FCSTD DOCUMENT  (FreeCAD 0.18R4 (GitTag))
Label: PLD1_stepper_side
License: All rights reserved
LicenseURL: http://en.wikipedia.org/wiki/All_rights_reserved
objects: Sketcher::SketchObject×1, PartDesign::Body×1
note: 2 computed .brp shape members not serialized (recipe doc carries the construction recipe); baked Part::Feature solids carry a one-line shape summary decoded from their .brp

FEATURE [Sketcher::SketchObject] Sketch
  MapMode = 5
  Support = -> [XY_Plane]
  sketch-geometry (69):
    g0: LineSegment StartX=-44 StartY=101.225 StartZ=0 EndX=0 EndY=101.225 EndZ=0
    g1: LineSegment StartX=0 StartY=101.225 StartZ=0 EndX=0 EndY=-101.225 EndZ=0
    g2: LineSegment StartX=0 StartY=-101.225 StartZ=0 EndX=-44 EndY=-101.225 EndZ=0
    g3: LineSegment StartX=-44 StartY=-101.225 StartZ=0 EndX=-44 EndY=101.225 EndZ=0
    g4: LineSegment StartX=-120.788 StartY=76.56 StartZ=0 EndX=-44 EndY=76.56 EndZ=0
    g5: LineSegment StartX=-44 StartY=76.56 StartZ=0 EndX=-44 EndY=-76.55 EndZ=0
    g6: LineSegment StartX=-44 StartY=-76.55 StartZ=0 EndX=-120.788 EndY=-76.55 EndZ=0
    g7: LineSegment StartX=-120.788 StartY=-76.55 StartZ=0 EndX=-120.788 EndY=76.56 EndZ=0
    g8: LineSegment StartX=0 StartY=155.225 StartZ=0 EndX=150 EndY=155.225 EndZ=0
    g9: LineSegment StartX=150 StartY=155.225 StartZ=0 EndX=150 EndY=151.225 EndZ=0
    g10: LineSegment StartX=150 StartY=151.225 StartZ=0 EndX=0 EndY=151.225 EndZ=0
    g11: LineSegment StartX=0 StartY=151.225 StartZ=0 EndX=0 EndY=155.225 EndZ=0
    g12: LineSegment StartX=-44 StartY=95.225 StartZ=0 EndX=0 EndY=95.225 EndZ=0
    g13: LineSegment StartX=0 StartY=95.225 StartZ=0 EndX=0 EndY=87.225 EndZ=0
    g14: LineSegment StartX=0 StartY=87.225 StartZ=0 EndX=-44 EndY=87.225 EndZ=0
    g15: LineSegment StartX=-44 StartY=87.225 StartZ=0 EndX=-44 EndY=95.225 EndZ=0
    g16: LineSegment StartX=0 StartY=66.725 StartZ=0 EndX=94 EndY=66.725 EndZ=0
    g17: LineSegment StartX=94 StartY=66.725 StartZ=0 EndX=94 EndY=31.725 EndZ=0
    g18: LineSegment StartX=94 StartY=31.725 StartZ=0 EndX=0 EndY=31.725 EndZ=0
    g19: LineSegment StartX=0 StartY=31.725 StartZ=0 EndX=0 EndY=66.725 EndZ=0
    g20: LineSegment StartX=94 StartY=52.225 StartZ=0 EndX=97 EndY=52.225 EndZ=0
    g21: LineSegment StartX=97 StartY=52.225 StartZ=0 EndX=97 EndY=46.225 EndZ=0
    g22: LineSegment StartX=97 StartY=46.225 StartZ=0 EndX=94 EndY=46.225 EndZ=0
    g23: LineSegment StartX=94 StartY=46.225 StartZ=0 EndX=94 EndY=52.225 EndZ=0
    g24: LineSegment StartX=97 StartY=59.225 StartZ=0 EndX=127 EndY=59.225 EndZ=0
    g25: LineSegment StartX=127 StartY=59.225 StartZ=0 EndX=127 EndY=39.225 EndZ=0
    g26: LineSegment StartX=127 StartY=39.225 StartZ=0 EndX=97 EndY=39.225 EndZ=0
    g27: LineSegment StartX=97 StartY=39.225 StartZ=0 EndX=97 EndY=59.225 EndZ=0
    g28: LineSegment StartX=135.919 StartY=67.225 StartZ=0 EndX=141.117 EndY=67.225 EndZ=0
    g29: LineSegment StartX=141.117 StartY=67.225 StartZ=0 EndX=141.117 EndY=31.225 EndZ=0
    g30: LineSegment StartX=141.117 StartY=31.225 StartZ=0 EndX=135.919 EndY=31.225 EndZ=0
    g31: LineSegment StartX=135.919 StartY=31.225 StartZ=0 EndX=135.919 EndY=67.225 EndZ=0
    g32: LineSegment StartX=135.919 StartY=142.225 StartZ=0 EndX=141.117 EndY=142.225 EndZ=0
    g33: LineSegment StartX=141.117 StartY=142.225 StartZ=0 EndX=141.117 EndY=67.225 EndZ=0
    g34: LineSegment StartX=141.117 StartY=67.225 StartZ=0 EndX=135.919 EndY=67.225 EndZ=0
    g35: LineSegment StartX=135.919 StartY=67.225 StartZ=0 EndX=135.919 EndY=142.225 EndZ=0
    g36: LineSegment StartX=96.6033 StartY=114.725 StartZ=0 EndX=126.603 EndY=114.725 EndZ=0
    g37: LineSegment StartX=126.603 StartY=114.725 StartZ=0 EndX=126.603 EndY=94.725 EndZ=0
    g38: LineSegment StartX=126.603 StartY=94.725 StartZ=0 EndX=96.6033 EndY=94.725 EndZ=0
    g39: LineSegment StartX=96.6033 StartY=94.725 StartZ=0 EndX=96.6033 EndY=114.725 EndZ=0
    g40: LineSegment StartX=43.1033 StartY=125.725 StartZ=0 EndX=93.6033 EndY=125.725 EndZ=0
    g41: LineSegment StartX=93.6033 StartY=125.725 StartZ=0 EndX=93.6033 EndY=83.725 EndZ=0
    g42: LineSegment StartX=93.6033 StartY=83.725 StartZ=0 EndX=43.1033 EndY=83.725 EndZ=0
    g43: LineSegment StartX=43.1033 StartY=83.725 StartZ=0 EndX=43.1033 EndY=125.725 EndZ=0
    g44: LineSegment StartX=150 StartY=151.225 StartZ=0 EndX=146 EndY=151.225 EndZ=0
    g45: LineSegment StartX=146 StartY=151.225 StartZ=0 EndX=146 EndY=21.225 EndZ=0
    g46: LineSegment StartX=146 StartY=21.225 StartZ=0 EndX=150 EndY=21.225 EndZ=0
    g47: LineSegment StartX=150 StartY=21.225 StartZ=0 EndX=150 EndY=151.225 EndZ=0
    g48: LineSegment StartX=43.1033 StartY=135.725 StartZ=0 EndX=93.6033 EndY=135.725 EndZ=0
    g49: LineSegment StartX=93.6033 StartY=135.725 StartZ=0 EndX=93.6033 EndY=125.725 EndZ=0
    g50: LineSegment StartX=93.6033 StartY=125.725 StartZ=0 EndX=43.1033 EndY=125.725 EndZ=0
    g51: LineSegment StartX=43.1033 StartY=125.725 StartZ=0 EndX=43.1033 EndY=135.725 EndZ=0
    g52: LineSegment StartX=44.3291 StartY=151.225 StartZ=0 EndX=44.3291 EndY=135.725 EndZ=0
    g53: LineSegment StartX=-103.974 StartY=186.345 StartZ=0 EndX=-68.9742 EndY=186.345 EndZ=0
    g54: LineSegment StartX=-68.9742 StartY=186.345 StartZ=0 EndX=-68.9742 EndY=130.045 EndZ=0
    g55: LineSegment StartX=-68.9742 StartY=130.045 StartZ=0 EndX=-103.974 EndY=130.045 EndZ=0
    g56: LineSegment StartX=-103.974 StartY=130.045 StartZ=0 EndX=-103.974 EndY=186.345 EndZ=0
    g57: LineSegment StartX=-82.7742 StartY=130.045 StartZ=0 EndX=-67.7742 EndY=130.045 EndZ=0
    g58: LineSegment StartX=-67.7742 StartY=130.045 StartZ=0 EndX=-67.7742 EndY=119.045 EndZ=0
    g59: LineSegment StartX=-67.7742 StartY=119.045 StartZ=0 EndX=-82.7742 EndY=119.045 EndZ=0
    g60: LineSegment StartX=-82.7742 StartY=119.045 StartZ=0 EndX=-82.7742 EndY=130.045 EndZ=0
    g61: LineSegment StartX=-218.667 StartY=182.94 StartZ=0 EndX=-118.667 EndY=182.94 EndZ=0
    g62: LineSegment StartX=-118.667 StartY=182.94 StartZ=0 EndX=-118.667 EndY=132.94 EndZ=0
    g63: LineSegment StartX=-118.667 StartY=132.94 StartZ=0 EndX=-218.667 EndY=132.94 EndZ=0
    g64: LineSegment StartX=-218.667 StartY=132.94 StartZ=0 EndX=-218.667 EndY=182.94 EndZ=0
    g65: LineSegment StartX=0 StartY=81.225 StartZ=0 EndX=4 EndY=81.225 EndZ=0
    g66: LineSegment StartX=4 StartY=81.225 StartZ=0 EndX=4 EndY=151.225 EndZ=0
    g67: LineSegment StartX=4 StartY=151.225 StartZ=0 EndX=0 EndY=151.225 EndZ=0
    g68: LineSegment StartX=0 StartY=151.225 StartZ=0 EndX=0 EndY=81.225 EndZ=0
  constraints (199):
    c: Coincident(g0,g1)
    c: Coincident(g1,g2)
    c: Coincident(g2,g3)
    c: Coincident(g3,g0)
    c: Horizontal(g0)
    c: Horizontal(g2)
    c: Vertical(g1)
    c: Vertical(g3)
    c: DistanceX(g0,g0) = 44
    c: DistanceX(g-1,g0) = 0
    c: DistanceY(g2,g0) = 202.45  '202.45'
    c: DistanceY(g1,g-1) = 101.225
    c: Coincident(g4,g5)
    c: Coincident(g5,g6)
    c: Coincident(g6,g7)
    c: Coincident(g7,g4)
    c: Horizontal(g4)
    c: Horizontal(g6)
    c: Vertical(g5)
    c: Vertical(g7)
    c: DistanceY(g6,g4) = 153.11
    c: DistanceX(g5,g2) = 0
    c: DistanceY(g6,g-1) = 76.55
    c: Coincident(g8,g9)
    c: Coincident(g9,g10)
    c: Coincident(g10,g11)
    c: Coincident(g11,g8)
    c: Horizontal(g8)
    c: Horizontal(g10)
    c: Vertical(g9)
    c: Vertical(g11)
    c: Coincident(g12,g13)
    c: Coincident(g13,g14)
    c: Coincident(g14,g15)
    c: Coincident(g15,g12)
    c: Horizontal(g12)
    c: Horizontal(g14)
    c: Vertical(g13)
    c: Vertical(g15)
    c: DistanceY(g13,g12) = 8
    c: DistanceY(g12,g0) = 6
    c: DistanceX(g12,g0) = 0
    c: DistanceX(g0,g12) = 0
    c: DistanceY(g9,g8) = 4
    c: DistanceY(g0,g10) = 50
    c: Coincident(g16,g17)
    c: Coincident(g17,g18)
    c: Coincident(g18,g19)
    c: Coincident(g19,g16)
    c: Horizontal(g16)
    c: Horizontal(g18)
    c: Vertical(g17)
    c: Vertical(g19)
    c: DistanceX(g13,g16) = 0
    c: DistanceY(g17,g16) = 35
    c: DistanceY(g16,g13) = 20.5
    c: DistanceX(g18,g17) = 94
    c: Coincident(g20,g21)
    c: Coincident(g21,g22)
    c: Coincident(g22,g23)
    c: Coincident(g23,g20)
    c: Horizontal(g20)
    c: Horizontal(g22)
    c: Vertical(g21)
    c: Vertical(g23)
    c: DistanceY(g21,g20) = 6
    c: DistanceX(g20,g20) = 3
    c: DistanceY(g20,g16) = 14.5
    c: DistanceX(g16,g20) = 0
    c: Coincident(g24,g25)
    c: Coincident(g25,g26)
    c: Coincident(g26,g27)
    c: Coincident(g27,g24)
    c: Horizontal(g24)
    c: Horizontal(g26)
    c: Vertical(g25)
    c: Vertical(g27)
    c: DistanceX(g24,g24) = 30
    c: DistanceY(g25,g24) = 20
    c: DistanceX(g20,g24) = 0
    c: DistanceY(g20,g24) = 7
    c: Coincident(g28,g29)
    c: Coincident(g29,g30)
    c: Coincident(g30,g31)
    c: Coincident(g31,g28)
    c: Horizontal(g28)
    c: Horizontal(g30)
    c: Vertical(g29)
    c: Vertical(g31)
    c: Coincident(g32,g33)
    c: Coincident(g33,g34)
    c: Coincident(g34,g35)
    c: Coincident(g35,g32)
    c: Horizontal(g32)
    c: Horizontal(g34)
    c: Vertical(g33)
    c: Vertical(g35)
    c: DistanceY(g29,g28) = 36
    c: DistanceY(g33,g32) = 75
    c: DistanceX(g33,g28) = 0
    c: DistanceY(g33,g28) = 0
    c: DistanceX(g34,g28) = 0
    c: DistanceY(g30,g25) = 8
    c: Coincident(g36,g37)
    c: Coincident(g37,g38)
    c: Coincident(g38,g39)
    c: Coincident(g39,g36)
    c: Horizontal(g36)
    c: Horizontal(g38)
    c: Vertical(g37)
    c: Vertical(g39)
    c: DistanceX(g38,g37) = 30
    c: DistanceY(g37,g36) = 20
    c: Coincident(g40,g41)
    c: Coincident(g41,g42)
    c: Coincident(g42,g43)
    c: Coincident(g43,g40)
    c: Horizontal(g40)
    c: Horizontal(g42)
    c: Vertical(g41)
    c: Vertical(g43)
    c: DistanceY(g42,g40) = 42
    c: DistanceX(g40,g40) = 50.5
    c: Coincident(g44,g45)
    c: Coincident(g45,g46)
    c: Coincident(g46,g47)
    c: Coincident(g47,g44)
    c: Horizontal(g44)
    c: Horizontal(g46)
    c: Vertical(g45)
    c: Vertical(g47)
    c: DistanceX(g45,g46) = 4
    c: DistanceX(g44,g9) = 0
    c: DistanceY(g44,g9) = 0
    c: DistanceX(g40,g36) = 3
    c: DistanceY(g41,g38) = 11
    c: Coincident(g48,g49)
    c: Coincident(g49,g50)
    c: Coincident(g50,g51)
    c: Coincident(g51,g48)
    c: Horizontal(g48)
    c: Horizontal(g50)
    c: Vertical(g49)
    c: Vertical(g51)
    c: DistanceY(g49,g48) = 10
    c: DistanceY(g40,g49) = 0
    c: DistanceX(g50,g40) = 0
    c: DistanceX(g40,g49) = 0
    c: DistanceY(g36,g32) = 27.5
    c: Parallel(g52,g45)
    c: Coincident(g53,g54)
    c: Coincident(g54,g55)
    c: Coincident(g55,g56)
    c: Coincident(g56,g53)
    c: Horizontal(g53)
    c: Horizontal(g55)
    c: Vertical(g54)
    c: Vertical(g56)
    c: DistanceX(g53,g53) = 35
    c: DistanceY(g54,g53) = 56.3
    c: DistanceY(g48,g52) = 0
    c: DistanceY(g52,g44) = 0
    c: Coincident(g57,g58)
    c: Coincident(g58,g59)
    c: Coincident(g59,g60)
    c: Coincident(g60,g57)
    c: Horizontal(g57)
    c: Horizontal(g59)
    c: Vertical(g58)
    c: Vertical(g60)
    c: DistanceY(g58,g57) = 11
    c: DistanceX(g59,g58) = 15
    c: DistanceY(g54,g57) = 0
    c: Coincident(g61,g62)
    c: Coincident(g62,g63)
    c: Coincident(g63,g64)
    c: Coincident(g64,g61)
    c: Horizontal(g61)
    c: Horizontal(g63)
    c: Vertical(g62)
    c: Vertical(g64)
    c: DistanceX(g61,g61) = 100
    c: DistanceY(g46,g9) = 130
    c: DistanceX(g54,g57) = 1.2
    c: Coincident(g65,g66)
    c: Coincident(g66,g67)
    c: Coincident(g67,g68)
    c: Coincident(g68,g65)
    c: Horizontal(g65)
    c: Horizontal(g67)
    c: Vertical(g66)
    c: Vertical(g68)
    c: DistanceX(g65,g65) = 4
    c: DistanceX(g67,g10) = 0
    c: DistanceY(g67,g10) = 0
    c: DistanceX(g0,g65) = 0
    c: DistanceX(g8,g8) = 150
    c: DistanceY(g62,g61) = 50
    c: DistanceY(g65,g66) = 70
FEATURE [PartDesign::Body] Body
  Group = -> [Sketch]
  Origin = -> Origin
